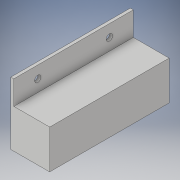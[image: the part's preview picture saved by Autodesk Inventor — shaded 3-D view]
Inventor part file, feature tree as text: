
AUTODESK INVENTOR PART (.ipt)
format: ipt  version: 2017 SP1 (Build 210196100, 196)  size: 125,440 bytes
history: native  units: in
note: dims shown in document units (in); Inventor stores cm internally (conversion verified against a paired STEP export)
features: sketch x4, extrude x3, hole x1
ambient origin geometry x8: Origin, YZ Plane, XZ Plane, XY Plane, X Axis, Y Axis, Z Axis, Center Point
bodies: Solid1 (feature_tree)
feature tree (8):
  extrude  "Extrusion1"  Depth=0.125in
  extrude  "Extrusion2"  Depth=1.5in
  extrude  "Extrusion3"  Depth=1.0in
  hole  "Hole1"  [1 undecoded]
  sketch  "Sketch1"  dims[d0=0.125in d1=0.125in]
  sketch  "Sketch2"  dims[d2=0.125in d3=1.5in]
  sketch  "Sketch3"  dims[d4=1.5in d5=1.0in]
  sketch  "Sketch4"  dims[d6=5.0in d7=0.0in d8=0.125in d9=0.0in d10=0.125in d11=0.0in d12=3.0in d13=1.0in d14=0.266in d15=0.75in d16=0.507in d17=0.25in d18=0.5635in d19=1.0in d20=0.8108in]
note: 1 required parameter value undecoded (feature->parameter linkage not recoverable at this tier; creation-order binding heuristic only, values carry confidence <= 0.55)
